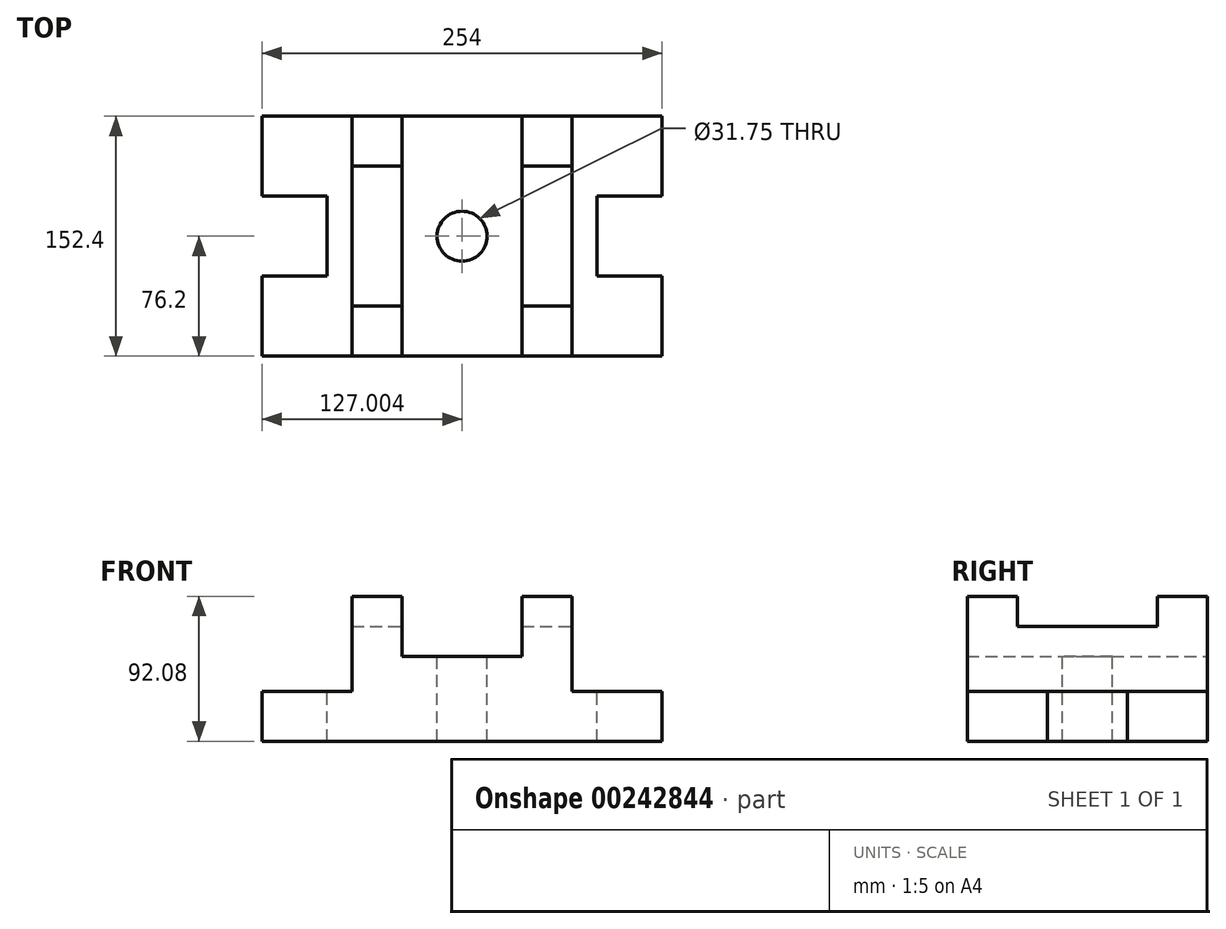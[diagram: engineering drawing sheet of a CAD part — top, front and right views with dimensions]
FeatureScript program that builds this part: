
annotation { "Feature Type Name" : "Feature", "Feature Type Description" : "" }
export const myFeature = defineFeature(function(context is Context, id is Id, definition is map)
    precondition{}
    {
        {
            var Q0;
            Q0=qCreatedBy(makeId("Front.planeOp"),FACE);
            var sketch = newSketch(context, id + "F0", { "sketchPlane" : qUnion([Q0])});
            skLineSegment(sketch, "E0", {"start": v(0, 0) * mm, "end": v(-30.44, 0) * mm});
            skLineSegment(sketch, "E1", {"start": v(-30.44, 0) * mm, "end": v(45.76, 0) * mm});
            skLineSegment(sketch, "E2", {"start": v(45.76, 0) * mm, "end": v(45.76, 38.1) * mm});
            skLineSegment(sketch, "E3", {"start": v(-30.44, 0) * mm, "end": v(-30.44, 38.1) * mm});
            skLineSegment(sketch, "E4", {"start": v(-30.44, 38.1) * mm, "end": v(-62.19, 38.1) * mm});
            skLineSegment(sketch, "E5", {"start": v(45.76, 38.1) * mm, "end": v(77.51, 38.1) * mm});
            skLineSegment(sketch, "E6", {"start": v(-62.19, 38.1) * mm, "end": v(-62.19, -22.23) * mm});
            skLineSegment(sketch, "E7", {"start": v(-62.19, -22.23) * mm, "end": v(-119.34, -22.23) * mm});
            skLineSegment(sketch, "E8", {"start": v(-119.34, -22.23) * mm, "end": v(-119.34, -53.98) * mm});
            skLineSegment(sketch, "E9", {"start": v(-119.34, -53.98) * mm, "end": v(134.66, -53.97) * mm});
            skLineSegment(sketch, "E10", {"start": v(134.66, -53.97) * mm, "end": v(134.66, -22.22) * mm});
            skLineSegment(sketch, "E11", {"start": v(77.51, -22.22) * mm, "end": v(77.51, 38.1) * mm});
            skLineSegment(sketch, "E12", {"start": v(77.51, -22.22) * mm, "end": v(134.66, -22.22) * mm});
            skSolve(sketch);
        }
        {
            var Q0;
            {var subQ2=sQuery(id+"F0.wireOp",EDGE,"E2");Q0=makeQuery(id+"F0.imprint","IMPRINT",FACE,{"disambiguationData":[TD([[makeQuery(id+"F0.imprint","IMPRINT",EDGE,{"derivedFrom":subQ2}),-1.0]])]});}
            extrude(context, id + "F1", {"entities" : qUnion([Q0]), "depth" : 152.4 * mm});
        }
        {
            var Q0;
            Q0=makeQuery(id+"F1.opExtrude","SWEPT_FACE",FACE,{"disambiguationData":[OSD([sQuery(id+"F0.wireOp",EDGE,"E11")])]});
            var sketch = newSketch(context, id + "F2", { "sketchPlane" : qUnion([Q0])});
            skLineSegment(sketch, "E13", {"start": v(-120.65, 38.1) * mm, "end": v(-120.65, 19.05) * mm});
            skLineSegment(sketch, "E14", {"start": v(-120.65, 19.05) * mm, "end": v(-31.75, 19.05) * mm});
            skLineSegment(sketch, "E15", {"start": v(-31.75, 19.05) * mm, "end": v(-31.75, 38.1) * mm});
            skSolve(sketch);
        }
        {
            var Q0;
            {var subQ0=sQuery(id+"F2.wireOp",EDGE,"E13");Q0=makeQuery(id+"F2.imprint","IMPRINT",FACE,{"disambiguationData":[TD([[makeQuery(id+"F2.imprint","IMPRINT",EDGE,{"derivedFrom":subQ0}),1.0]])]});}
            extrude(context, id + "F3", {"entities" : qUnion([Q0]), "operationType" : NewBodyOperationType.REMOVE, "oppositeDirection" : true, "depth" : 152.4 * mm});
        }
        {
            var Q0;
            Q0=makeQuery(id+"F1.opExtrude","SWEPT_FACE",FACE,{"disambiguationData":[OSD([sQuery(id+"F0.wireOp",EDGE,"E7")])]});
            var sketch = newSketch(context, id + "F4", { "sketchPlane" : qUnion([Q0])});
            skLineSegment(sketch, "E16", {"start": v(-119.34, -50.8) * mm, "end": v(-78.06, -50.8) * mm});
            skLineSegment(sketch, "E17", {"start": v(-78.06, -50.8) * mm, "end": v(-78.06, -101.6) * mm});
            skLineSegment(sketch, "E18", {"start": v(-119.34, -101.6) * mm, "end": v(-78.06, -101.6) * mm});
            skSolve(sketch);
        }
        {
            var Q0;
            Q0 = qSketchRegion(id + "F4", true);
            var Q1;
            {var subQ0=sQuery(id+"F4.wireOp",EDGE,"E16");Q1=makeQuery(id+"F4.imprint","IMPRINT",FACE,{"disambiguationData":[TD([[makeQuery(id+"F4.imprint","IMPRINT",EDGE,{"derivedFrom":subQ0}),-1.0]])]});}
            extrude(context, id + "F5", {"entities" : qUnion([Q0, Q1]), "operationType" : NewBodyOperationType.REMOVE, "oppositeDirection" : true, "depth" : 50.8 * mm});
        }
        {
            var Q0;
            Q0=makeQuery(id+"F1.opExtrude","SWEPT_FACE",FACE,{"disambiguationData":[OSD([sQuery(id+"F0.wireOp",EDGE,"E12")])]});
            var sketch = newSketch(context, id + "F6", { "sketchPlane" : qUnion([Q0])});
            skLineSegment(sketch, "E19", {"start": v(134.66, -50.8) * mm, "end": v(93.39, -50.8) * mm});
            skLineSegment(sketch, "E20", {"start": v(93.39, -50.8) * mm, "end": v(93.39, -101.6) * mm});
            skLineSegment(sketch, "E21", {"start": v(93.39, -101.6) * mm, "end": v(134.66, -101.6) * mm});
            skSolve(sketch);
        }
        {
            var Q0;
            {var subQ0=sQuery(id+"F6.wireOp",EDGE,"E19");Q0=makeQuery(id+"F6.imprint","IMPRINT",FACE,{"disambiguationData":[TD([[makeQuery(id+"F6.imprint","IMPRINT",EDGE,{"derivedFrom":subQ0}),1.0]])]});}
            extrude(context, id + "F7", {"entities" : qUnion([Q0]), "operationType" : NewBodyOperationType.REMOVE, "oppositeDirection" : true, "depth" : 50.8 * mm});
        }
        {
            var Q0;
            Q0=makeQuery(id+"F1.opExtrude","SWEPT_FACE",FACE,{"disambiguationData":[OSD([sQuery(id+"F0.wireOp",EDGE,"E1")])]});
            var sketch = newSketch(context, id + "F8", { "sketchPlane" : qUnion([Q0])});
            skCircle(sketch, "E22", {"center": v(7.66, -76.2) * mm, "radius": 15.88 * mm});
            skSolve(sketch);
        }
        {
            var Q0;
            Q0=makeQuery(id+"F8.imprint","IMPRINT",FACE,{"disambiguationData":[TD([[makeQuery(id+"F8.imprint","IMPRINT",EDGE,{"derivedFrom":sQuery(id+"F8.wireOp",EDGE,"E22")}),1.0]])]});
            extrude(context, id + "F9", {"entities" : qUnion([Q0]), "operationType" : NewBodyOperationType.REMOVE, "oppositeDirection" : true, "depth" : 152.4 * mm});
        }
    });
